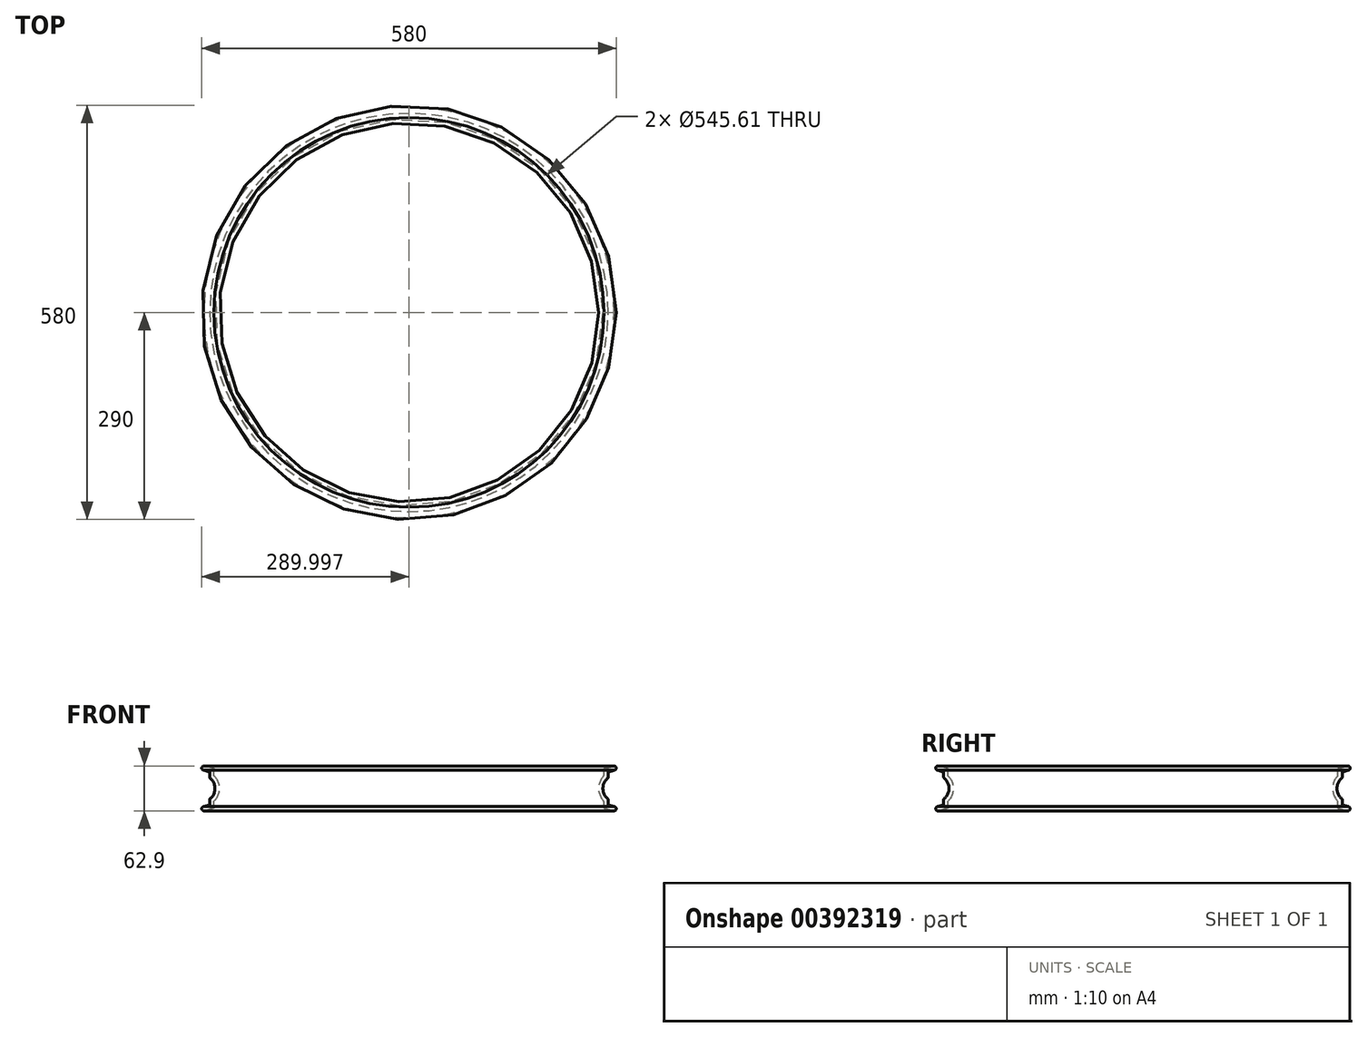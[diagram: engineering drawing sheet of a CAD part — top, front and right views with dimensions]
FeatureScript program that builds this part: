
annotation { "Feature Type Name" : "Feature", "Feature Type Description" : "" }
export const myFeature = defineFeature(function(context is Context, id is Id, definition is map)
    precondition{}
    {
        {
            var Q0;
            Q0=qCreatedBy(makeId("Front.planeOp"),FACE);
            var sketch = newSketch(context, id + "F0", { "sketchPlane" : qUnion([Q0])});
            skLineSegment(sketch, "E0", {"start": v(17.63, 18.13) * mm, "end": v(17.63, 26.96) * mm});
            skLineSegment(sketch, "E1", {"start": v(16.9, 27.92) * mm, "end": v(4.25, 31.35) * mm});
            skLineSegment(sketch, "E2.0", {"start": v(10.9, 23.33) * mm, "end": v(3.17, 25.43) * mm});
            skLineSegment(sketch, "E3.0", {"start": v(11.63, 15.5) * mm, "end": v(11.63, 22.37) * mm});
            skLineSegment(sketch, "E4.MirrorCS", {"start": v(16.9, -27.92) * mm, "end": v(4.25, -31.35) * mm});
            skLineSegment(sketch, "E5.MirrorCS", {"start": v(10.9, -23.33) * mm, "end": v(3.17, -25.43) * mm});
            skLineSegment(sketch, "E6.MirrorCS", {"start": v(11.63, -15.5) * mm, "end": v(11.63, -22.37) * mm});
            skLineSegment(sketch, "E7.MirrorCS", {"start": v(17.63, -18.13) * mm, "end": v(17.63, -26.96) * mm});
            skArc(sketch, "E8", {"start": v(17.91, -17.44) * mm, "mid": v(25, 0) * mm, "end": v(17.91, 17.44) * mm});
            skArc(sketch, "E9", {"start": v(12, -14.73) * mm, "mid": v(19, 0) * mm, "end": v(12, 14.73) * mm});
            skPoint(sketch, "E10.visualSharp", {"position": v(11.63, 23.13) * mm});
            skArc(sketch, "E10.filletArc", {"start": v(11.63, 22.37) * mm, "mid": v(11.43, 22.98) * mm, "end": v(10.9, 23.33) * mm});
            skPoint(sketch, "E11.visualSharp", {"position": v(17.63, 27.72) * mm});
            skArc(sketch, "E11.filletArc", {"start": v(17.63, 26.96) * mm, "mid": v(17.43, 27.57) * mm, "end": v(16.9, 27.92) * mm});
            skPoint(sketch, "E12.visualSharp", {"position": v(17.63, 17.72) * mm});
            skArc(sketch, "E12.filletArc", {"start": v(17.63, 18.13) * mm, "mid": v(17.7, 17.76) * mm, "end": v(17.91, 17.44) * mm});
            skPoint(sketch, "E13.visualSharp", {"position": v(11.63, 15.02) * mm});
            skArc(sketch, "E13.filletArc", {"start": v(11.63, 15.5) * mm, "mid": v(11.73, 15.08) * mm, "end": v(12, 14.73) * mm});
            skPoint(sketch, "E14.visualSharp", {"position": v(17.63, -17.72) * mm});
            skArc(sketch, "E14.filletArc", {"start": v(17.91, -17.44) * mm, "mid": v(17.7, -17.76) * mm, "end": v(17.63, -18.13) * mm});
            skPoint(sketch, "E15.visualSharp", {"position": v(17.63, -27.72) * mm});
            skArc(sketch, "E15.filletArc", {"start": v(16.9, -27.92) * mm, "mid": v(17.43, -27.57) * mm, "end": v(17.63, -26.96) * mm});
            skPoint(sketch, "E16.visualSharp", {"position": v(11.63, -23.13) * mm});
            skArc(sketch, "E16.filletArc", {"start": v(10.9, -23.33) * mm, "mid": v(11.43, -22.98) * mm, "end": v(11.63, -22.37) * mm});
            skPoint(sketch, "E17.visualSharp", {"position": v(11.63, -15.02) * mm});
            skArc(sketch, "E17.filletArc", {"start": v(12, -14.73) * mm, "mid": v(11.73, -15.08) * mm, "end": v(11.63, -15.5) * mm});
            skArc(sketch, "E18", {"start": v(4.25, 31.35) * mm, "mid": v(0.49, 28.98) * mm, "end": v(3.17, 25.43) * mm});
            skArc(sketch, "E19.MirrorCS", {"start": v(4.25, -31.35) * mm, "mid": v(0.49, -28.98) * mm, "end": v(3.17, -25.43) * mm});
            skLineSegment(sketch, "E20", {"start": v(0.44, 33.12) * mm, "end": v(0.44, -32.65) * mm, "construction": true});
            skLineSegment(sketch, "E21.0", {"start": v(290.44, 33.12) * mm, "end": v(290.44, -32.65) * mm});
            skLineSegment(sketch, "E22.0", {"start": v(580.44, 33.12) * mm, "end": v(580.44, -32.65) * mm});
            skSolve(sketch);
        }
        {
            var Q0;
            Q0 = qSketchRegion(id + "F0", true);
            var Q1;
            Q1=sQuery(id+"F0.wireOp",EDGE,"E21.0");
            revolve(context, id + "F1", {"entities" : qUnion([Q0]), "axis" : qUnion([Q1]), "revolveType" : RevolveType.FULL});
        }
    });
